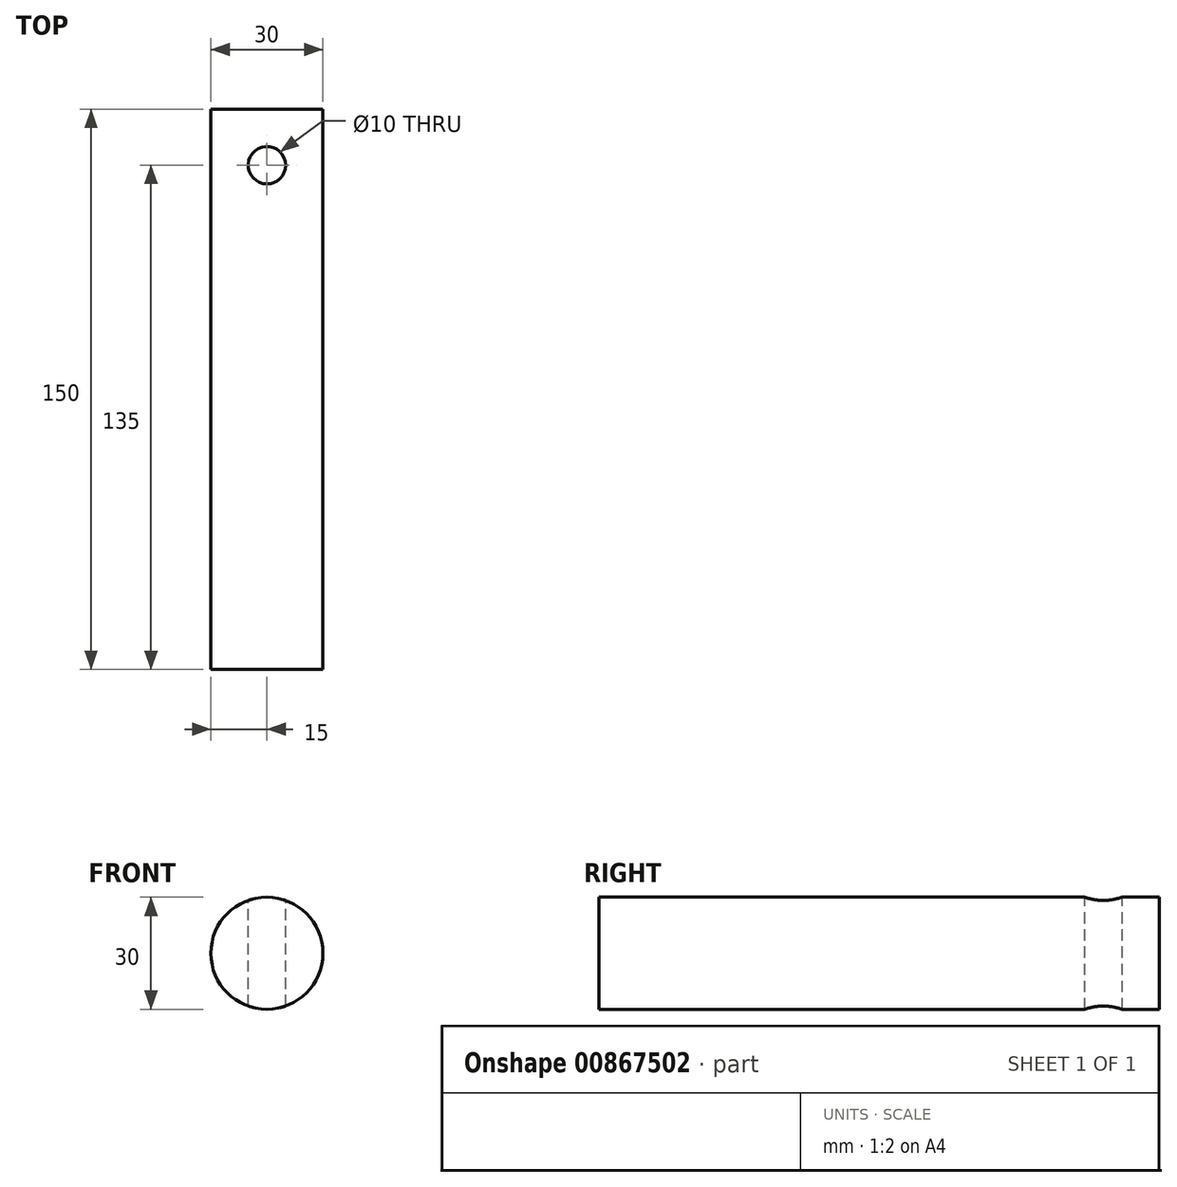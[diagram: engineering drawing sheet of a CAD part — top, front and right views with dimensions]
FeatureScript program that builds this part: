
annotation { "Feature Type Name" : "Feature", "Feature Type Description" : "" }
export const myFeature = defineFeature(function(context is Context, id is Id, definition is map)
    precondition{}
    {
        {
            var Q0;
            Q0=qCreatedBy(makeId("Front.planeOp"),FACE);
            var sketch = newSketch(context, id + "F0", { "sketchPlane" : qUnion([Q0])});
            skCircle(sketch, "E0", {"center": v(0, 0) * mm, "radius": 15 * mm});
            skSolve(sketch);
        }
        {
            var Q0;
            Q0=makeQuery(id+"F0.imprint","IMPRINT",FACE,{"disambiguationData":[TD([[makeQuery(id+"F0.imprint","IMPRINT",EDGE,{"derivedFrom":sQuery(id+"F0.wireOp",EDGE,"E0")}),-1.0]])]});
            var Q1;
            Q1=makeQuery(id+"F0.imprint","IMPRINT",FACE,{"disambiguationData":[TD([[makeQuery(id+"F0.imprint","IMPRINT",EDGE,{"derivedFrom":sQuery(id+"F0.wireOp",EDGE,"E0")}),1.0]])]});
            extrude(context, id + "F1", {"entities" : qUnion([Q0, Q1]), "depth" : 150 * mm, "offsetDistance" : 25 * mm});
        }
        {
            var Q0;
            Q0=qCreatedBy(makeId("Top.planeOp"),FACE);
            var sketch = newSketch(context, id + "F2", { "sketchPlane" : qUnion([Q0])});
            skCircle(sketch, "E1", {"center": v(0, 0) * mm, "radius": 15 * mm});
            skCircle(sketch, "E2", {"center": v(0, -15) * mm, "radius": 5 * mm});
            skSolve(sketch);
        }
        {
            var Q0;
            {var subQ0=sQuery(id+"F2.wireOp",EDGE,"E2");var subQ1=sQuery(id+"F2.wireOp",EDGE,"E1");var subQ2=makeQuery(id+"F2.imprint","INTERSECT",VERTEX,{"disambiguationData":[OD(0.0)],"derivedFrom":[subQ1,subQ0]});Q0=makeQuery(id+"F2.imprint","IMPRINT",FACE,{"disambiguationData":[TD([[makeQuery(id+"F2.imprint","IMPRINT",EDGE,{"disambiguationData":[TD([[subQ2,-1.0]])],"derivedFrom":subQ1}),-1.0]])]});}
            var Q1;
            {var subQ0=sQuery(id+"F2.wireOp",EDGE,"E2");var subQ1=sQuery(id+"F2.wireOp",EDGE,"E1");var subQ2=makeQuery(id+"F2.imprint","INTERSECT",VERTEX,{"disambiguationData":[OD(0.0)],"derivedFrom":[subQ1,subQ0]});Q1=makeQuery(id+"F2.imprint","IMPRINT",FACE,{"disambiguationData":[TD([[makeQuery(id+"F2.imprint","IMPRINT",EDGE,{"disambiguationData":[TD([[subQ2,-1.0]])],"derivedFrom":subQ1}),1.0]])]});}
            extrude(context, id + "F3", {"entities" : qUnion([Q0, Q1]), "operationType" : NewBodyOperationType.REMOVE, "endBound" : BoundingType.SYMMETRIC, "oppositeDirection" : true, "depth" : 39.8 * mm, "offsetDistance" : 25 * mm});
        }
    });
